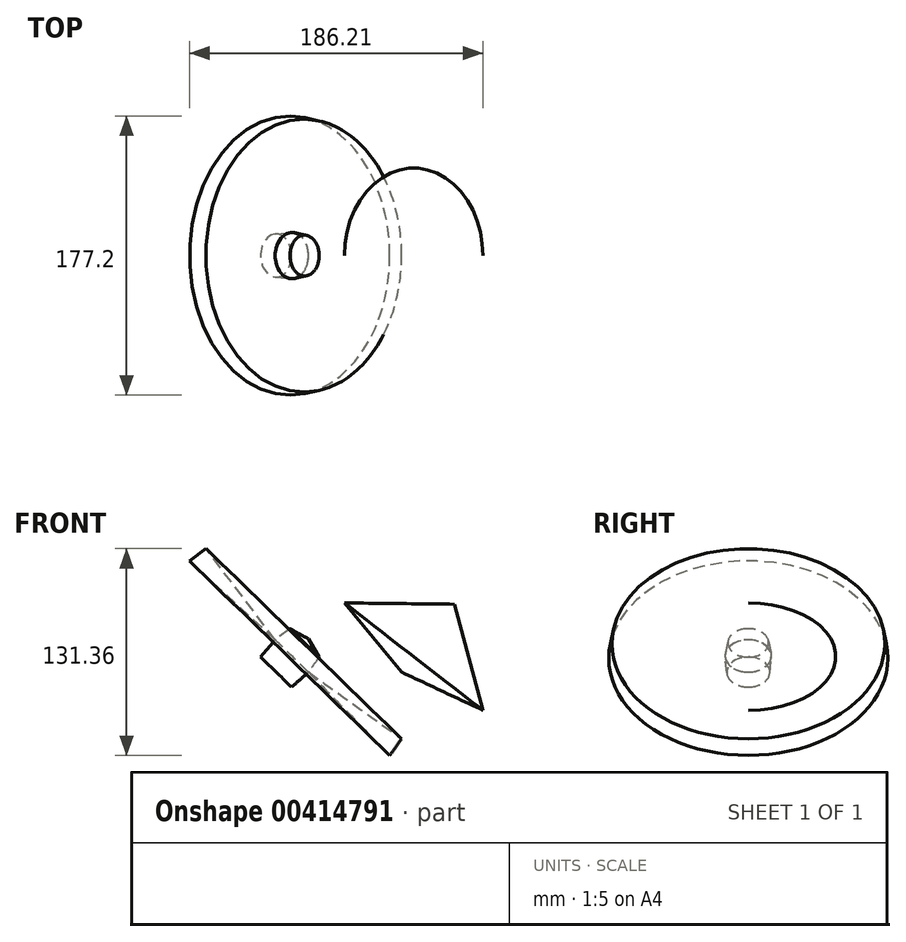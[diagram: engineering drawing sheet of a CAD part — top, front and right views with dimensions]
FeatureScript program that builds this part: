
annotation { "Feature Type Name" : "Feature", "Feature Type Description" : "" }
export const myFeature = defineFeature(function(context is Context, id is Id, definition is map)
    precondition{}
    {
        {
            var Q0;
            Q0=qCreatedBy(makeId("Front.planeOp"),FACE);
            var sketch = newSketch(context, id + "F0", { "sketchPlane" : qUnion([Q0])});
            skLineSegment(sketch, "E0", {"start": v(-36.28, 43.95) * mm, "end": v(0, 0) * mm});
            skLineSegment(sketch, "E1", {"start": v(0, 0) * mm, "end": v(33.45, 43.11) * mm});
            skLineSegment(sketch, "E2", {"start": v(33.45, 43.11) * mm, "end": v(-36.28, 43.95) * mm});
            skSolve(sketch);
        }
        {
            var Q0;
            Q0 = qSketchRegion(id + "F0", true);
            var Q1;
            Q1=sQuery(id+"F0.wireOp",EDGE,"E1");
            revolve(context, id + "F1", {"entities" : qUnion([Q0]), "axis" : qUnion([Q1]), "revolveType" : RevolveType.FULL});
        }
        {
            var Q0;
            Q0=qCreatedBy(makeId("Front.planeOp"),FACE);
            var sketch = newSketch(context, id + "F2", { "sketchPlane" : qUnion([Q0])});
            skLineSegment(sketch, "E3", {"start": v(0, -42.33) * mm, "end": v(-59.2, 0) * mm});
            skLineSegment(sketch, "E4", {"start": v(-59.2, 0) * mm, "end": v(-52.38, 9.54) * mm});
            skLineSegment(sketch, "E5", {"start": v(-52.38, 9.54) * mm, "end": v(-59.2, 21.1) * mm});
            skLineSegment(sketch, "E6", {"start": v(-59.2, 21.1) * mm, "end": v(-79.7, 0) * mm});
            skLineSegment(sketch, "E7", {"start": v(-79.7, 0) * mm, "end": v(-69.87, -9.55) * mm});
            skLineSegment(sketch, "E8", {"start": v(-69.87, -9.55) * mm, "end": v(-69.87, -9.55) * mm});
            skLineSegment(sketch, "E9", {"start": v(-69.87, -9.55) * mm, "end": v(-59.2, 0) * mm});
            skLineSegment(sketch, "E10", {"start": v(0, -42.33) * mm, "end": v(-7.56, -52.9) * mm});
            skLineSegment(sketch, "E11", {"start": v(-7.56, -52.9) * mm, "end": v(-59.2, 0) * mm});
            skSolve(sketch);
        }
        {
            var Q0;
            Q0=makeQuery(id+"F2.imprint","IMPRINT",FACE,{"disambiguationData":[TD([[makeQuery(id+"F2.imprint","IMPRINT",EDGE,{"derivedFrom":sQuery(id+"F2.wireOp",EDGE,"E3")}),1.0]])]});
            var Q1;
            Q1=makeQuery(id+"F2.imprint","IMPRINT",FACE,{"disambiguationData":[TD([[makeQuery(id+"F2.imprint","IMPRINT",EDGE,{"derivedFrom":sQuery(id+"F2.wireOp",EDGE,"E4")}),1.0]])]});
            var Q2;
            Q2=sQuery(id+"F2.wireOp",EDGE,"E6");
            revolve(context, id + "F3", {"entities" : qUnion([Q0, Q1]), "axis" : qUnion([Q2]), "revolveType" : RevolveType.FULL});
        }
    });
